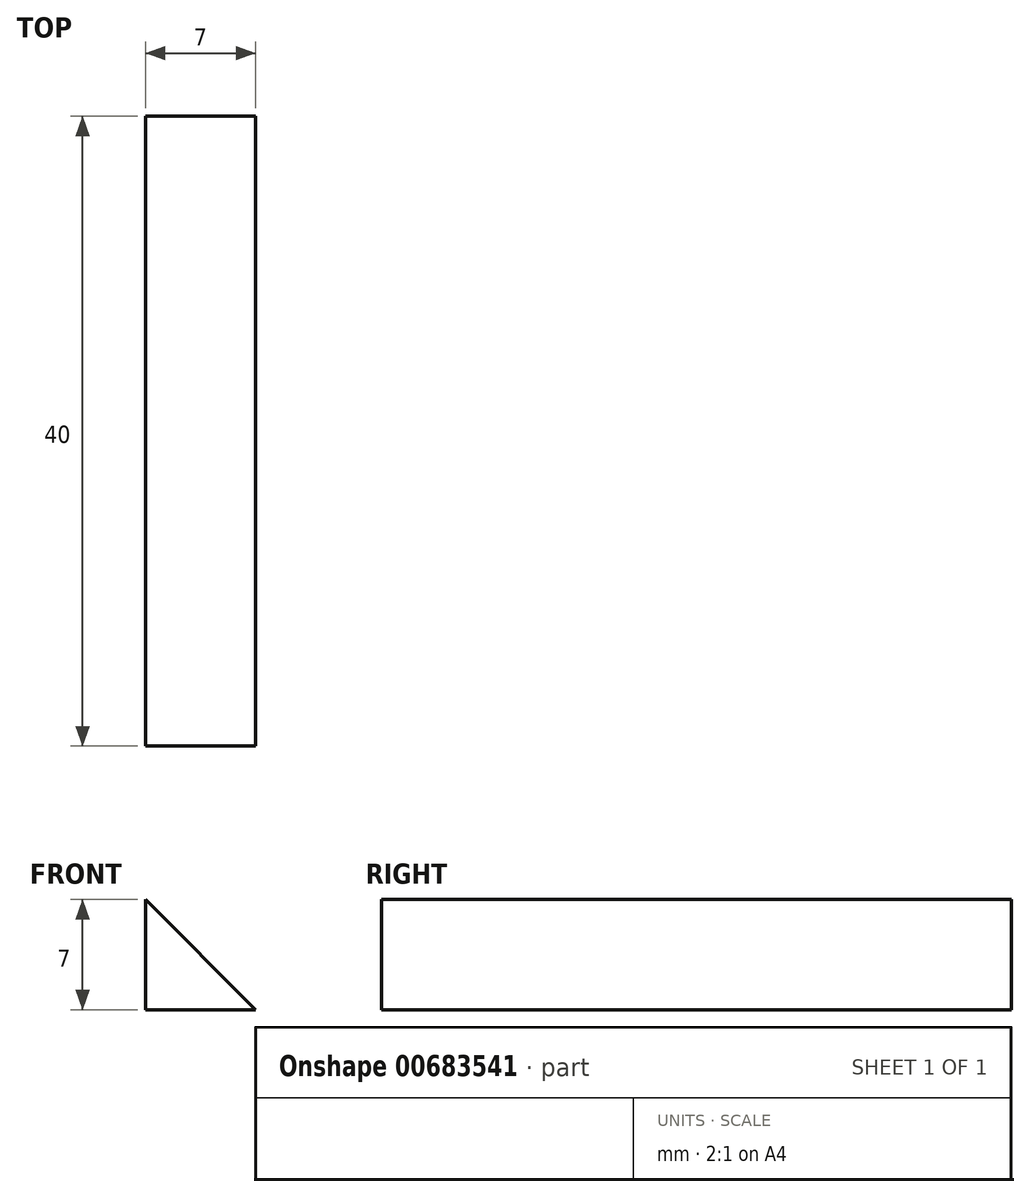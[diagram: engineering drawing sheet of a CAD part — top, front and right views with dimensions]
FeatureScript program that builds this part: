
annotation { "Feature Type Name" : "Feature", "Feature Type Description" : "" }
export const myFeature = defineFeature(function(context is Context, id is Id, definition is map)
    precondition{}
    {
        {
            var Q0;
            Q0=qCreatedBy(makeId("Front.planeOp"),FACE);
            var sketch = newSketch(context, id + "F0", { "sketchPlane" : qUnion([Q0])});
            skLineSegment(sketch, "E0", {"start": v(0, 7) * mm, "end": v(0, 0) * mm});
            skLineSegment(sketch, "E1", {"start": v(0, 0) * mm, "end": v(7, 0) * mm});
            skLineSegment(sketch, "E2", {"start": v(7, 0) * mm, "end": v(0, 7) * mm});
            skSolve(sketch);
        }
        {
            var Q0;
            Q0 = qSketchRegion(id + "F0", true);
            extrude(context, id + "F1", {"entities" : qUnion([Q0]), "endBound" : BoundingType.SYMMETRIC, "depth" : 40 * mm, "offsetDistance" : 25 * mm});
        }
    });
